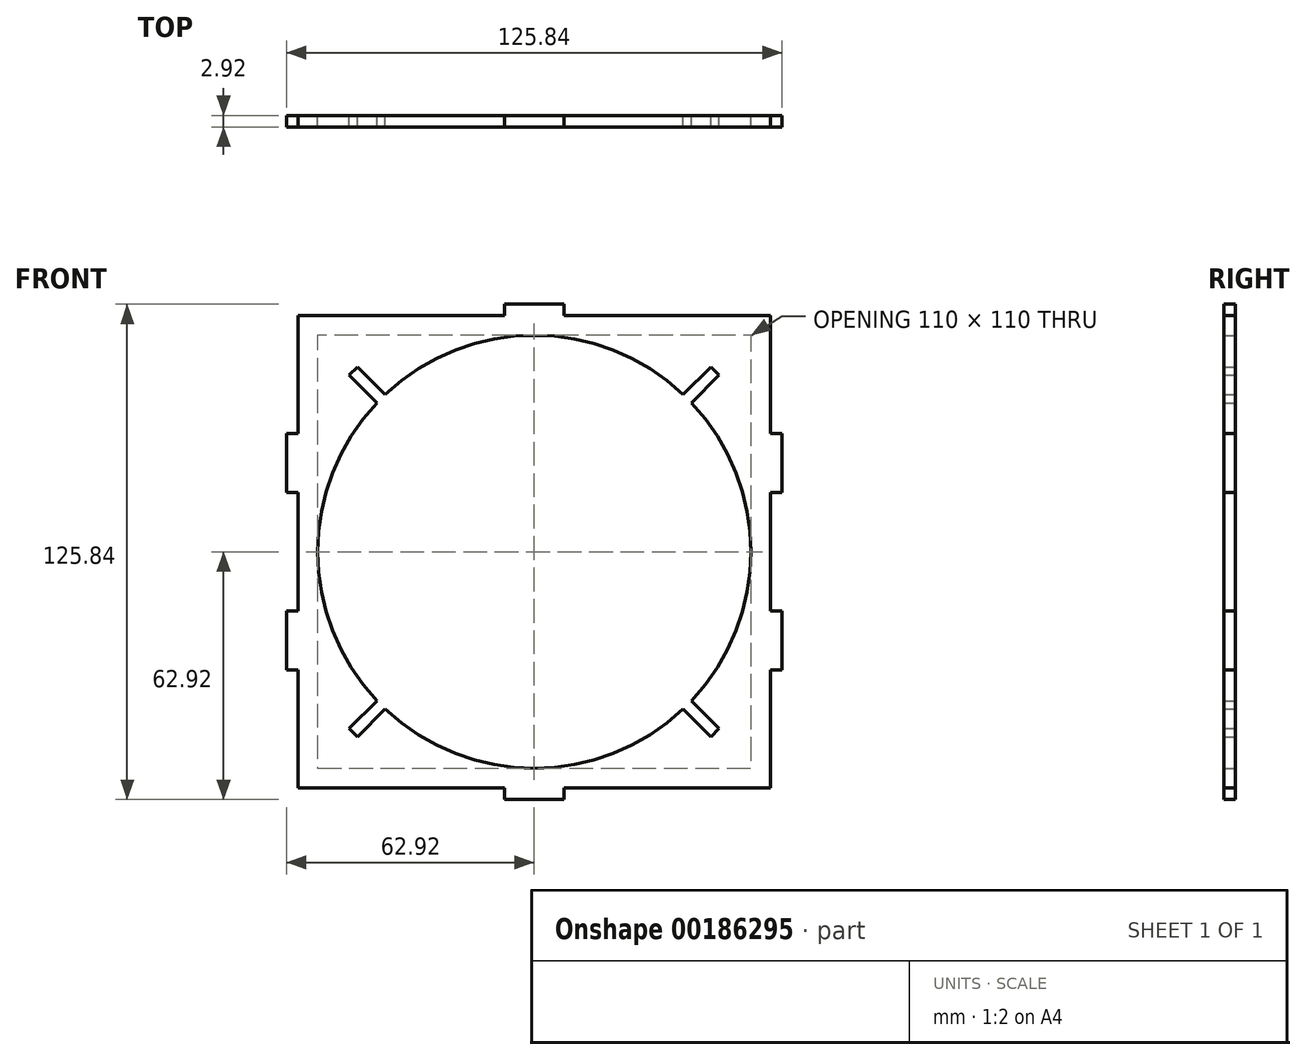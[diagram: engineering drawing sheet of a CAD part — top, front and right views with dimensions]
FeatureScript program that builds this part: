
annotation { "Feature Type Name" : "Feature", "Feature Type Description" : "" }
export const myFeature = defineFeature(function(context is Context, id is Id, definition is map)
    precondition{}
    {
        {
            assignVariable(context, id + "F0", {"name" : "e", "anyValue" : 2.92 * mm});
        }
        {
            var Q0;
            Q0=qCreatedBy(makeId("Front.planeOp"),FACE);
            var sketch = newSketch(context, id + "F1", { "sketchPlane" : qUnion([Q0])});
            skLineSegment(sketch, "E0.bottom", {"start": v(-60, 60) * mm, "end": v(-7.5, 60) * mm});
            skLineSegment(sketch, "E0.top", {"start": v(-60, 0) * mm, "end": v(0, 0) * mm, "construction": true});
            skLineSegment(sketch, "E0.left", {"start": v(-60, 60) * mm, "end": v(-60, 30) * mm});
            skLineSegment(sketch, "E0.right", {"start": v(0, 60) * mm, "end": v(0, 0) * mm, "construction": true});
            skLineSegment(sketch, "E1.bottom", {"start": v(-60, 30) * mm, "end": v(-62.92, 30) * mm});
            skLineSegment(sketch, "E1.top", {"start": v(-60, 15) * mm, "end": v(-62.92, 15) * mm});
            skLineSegment(sketch, "E1.right", {"start": v(-62.92, 30) * mm, "end": v(-62.92, 15) * mm});
            skLineSegment(sketch, "E2.trimOffspring", {"start": v(-60, 15) * mm, "end": v(-60, 0) * mm});
            skLineSegment(sketch, "E3.MirrorCS", {"start": v(60, 15) * mm, "end": v(60, 0) * mm});
            skLineSegment(sketch, "E4.MirrorCS", {"start": v(62.92, 30) * mm, "end": v(62.92, 15) * mm});
            skLineSegment(sketch, "E5.MirrorCS", {"start": v(60, 15) * mm, "end": v(62.92, 15) * mm});
            skLineSegment(sketch, "E6.MirrorCS", {"start": v(60, 30) * mm, "end": v(62.92, 30) * mm});
            skLineSegment(sketch, "E7.MirrorCS", {"start": v(60, 60) * mm, "end": v(7.5, 60) * mm});
            skLineSegment(sketch, "E8.MirrorCS", {"start": v(60, 60) * mm, "end": v(60, 30) * mm});
            skLineSegment(sketch, "E9.MirrorCS", {"start": v(-60, -15) * mm, "end": v(-60, 0) * mm});
            skLineSegment(sketch, "E10.MirrorCS", {"start": v(60, -15) * mm, "end": v(60, 0) * mm});
            skLineSegment(sketch, "E11.MirrorCS", {"start": v(60, -60) * mm, "end": v(60, -30) * mm});
            skLineSegment(sketch, "E12.MirrorCS", {"start": v(60, -60) * mm, "end": v(7.5, -60) * mm});
            skLineSegment(sketch, "E13.MirrorCS", {"start": v(60, -30) * mm, "end": v(62.92, -30) * mm});
            skLineSegment(sketch, "E14.MirrorCS", {"start": v(60, -15) * mm, "end": v(62.92, -15) * mm});
            skLineSegment(sketch, "E15.MirrorCS", {"start": v(62.92, -30) * mm, "end": v(62.92, -15) * mm});
            skLineSegment(sketch, "E16.MirrorCS", {"start": v(-60, -60) * mm, "end": v(-60, -30) * mm});
            skLineSegment(sketch, "E17.MirrorCS", {"start": v(-60, -60) * mm, "end": v(-7.5, -60) * mm});
            skLineSegment(sketch, "E18.MirrorCS", {"start": v(-60, -30) * mm, "end": v(-62.92, -30) * mm});
            skLineSegment(sketch, "E19.MirrorCS", {"start": v(-62.92, -30) * mm, "end": v(-62.92, -15) * mm});
            skLineSegment(sketch, "E20.MirrorCS", {"start": v(-60, -15) * mm, "end": v(-62.92, -15) * mm});
            skArc(sketch, "E21", {"start": v(-39.9, 37.84) * mm, "mid": v(-55, 0) * mm, "end": v(-39.9, -37.84) * mm});
            skLineSegment(sketch, "E22.top", {"start": v(-7.5, 62.92) * mm, "end": v(7.5, 62.92) * mm});
            skLineSegment(sketch, "E22.left", {"start": v(-7.5, 60) * mm, "end": v(-7.5, 62.92) * mm});
            skLineSegment(sketch, "E22.right", {"start": v(7.5, 60) * mm, "end": v(7.5, 62.92) * mm});
            skPoint(sketch, "E23.orphan", {"position": v(0, 60) * mm});
            skLineSegment(sketch, "E24.MirrorCS", {"start": v(7.5, -60) * mm, "end": v(7.5, -62.92) * mm});
            skLineSegment(sketch, "E25.MirrorCS", {"start": v(-7.5, -62.92) * mm, "end": v(7.5, -62.92) * mm});
            skLineSegment(sketch, "E26.MirrorCS", {"start": v(-7.5, -60) * mm, "end": v(-7.5, -62.92) * mm});
            skPoint(sketch, "E27.orphan", {"position": v(0, -60) * mm});
            skLineSegment(sketch, "E28", {"start": v(-60, 60) * mm, "end": v(0, 0) * mm, "construction": true});
            skLineSegment(sketch, "E29", {"start": v(-46.98, 44.92) * mm, "end": v(-44.92, 46.98) * mm});
            skLineSegment(sketch, "E30", {"start": v(-44.92, 46.98) * mm, "end": v(-37.84, 39.9) * mm});
            skLineSegment(sketch, "E31", {"start": v(-46.98, 44.92) * mm, "end": v(-39.9, 37.84) * mm});
            skPoint(sketch, "E32", {"position": v(-45.95, 45.95) * mm});
            skLineSegment(sketch, "E33.1.0", {"start": v(-44.92, -46.98) * mm, "end": v(-37.84, -39.9) * mm});
            skLineSegment(sketch, "E33.1.1", {"start": v(-44.92, -46.98) * mm, "end": v(-46.98, -44.92) * mm});
            skLineSegment(sketch, "E33.1.2", {"start": v(-46.98, -44.92) * mm, "end": v(-39.9, -37.84) * mm});
            skLineSegment(sketch, "E33.2.0", {"start": v(46.98, -44.92) * mm, "end": v(39.9, -37.84) * mm});
            skLineSegment(sketch, "E33.2.1", {"start": v(46.98, -44.92) * mm, "end": v(44.92, -46.98) * mm});
            skLineSegment(sketch, "E33.2.2", {"start": v(44.92, -46.98) * mm, "end": v(37.84, -39.9) * mm});
            skLineSegment(sketch, "E33.3.0", {"start": v(44.92, 46.98) * mm, "end": v(37.84, 39.9) * mm});
            skLineSegment(sketch, "E33.3.1", {"start": v(44.92, 46.98) * mm, "end": v(46.98, 44.92) * mm});
            skLineSegment(sketch, "E33.3.2", {"start": v(46.98, 44.92) * mm, "end": v(39.9, 37.84) * mm});
            skArc(sketch, "E34.trimOffspring", {"start": v(37.84, 39.9) * mm, "mid": v(0, 55) * mm, "end": v(-37.84, 39.9) * mm});
            skArc(sketch, "E35.trimOffspring", {"start": v(39.9, -37.84) * mm, "mid": v(55, 0) * mm, "end": v(39.9, 37.84) * mm});
            skArc(sketch, "E36.trimOffspring", {"start": v(-37.84, -39.9) * mm, "mid": v(0, -55) * mm, "end": v(37.84, -39.9) * mm});
            skSolve(sketch);
        }
        {
            var Q0;
            Q0 = qSketchRegion(id + "F1", true);
            extrude(context, id + "F2", {"entities" : qUnion([Q0]), "depth" : getVariable(context, 'e')});
        }
    });
